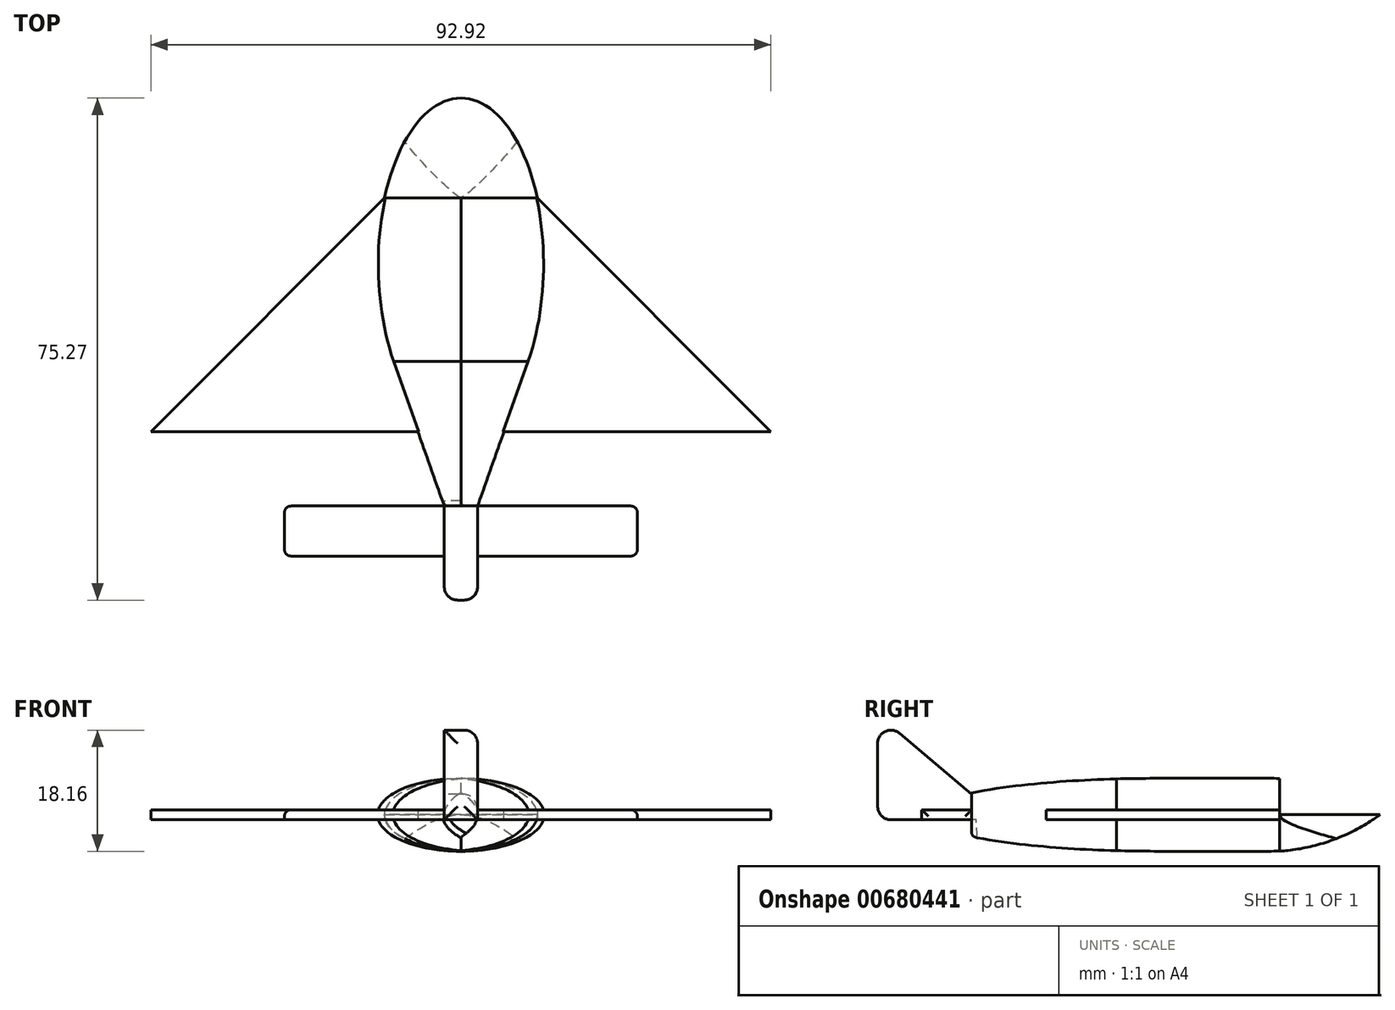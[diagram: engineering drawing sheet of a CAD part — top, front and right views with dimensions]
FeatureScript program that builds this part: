
annotation { "Feature Type Name" : "Feature", "Feature Type Description" : "" }
export const myFeature = defineFeature(function(context is Context, id is Id, definition is map)
    precondition{}
    {
        {
            var Q0;
            Q0=qCreatedBy(makeId("Top.planeOp"),FACE);
            var sketch = newSketch(context, id + "F0", { "sketchPlane" : qUnion([Q0])});
            skLineSegment(sketch, "E0", {"start": v(0, -25) * mm, "end": v(0, -47.8) * mm, "construction": true});
            skLineSegment(sketch, "E1", {"start": v(-2.5, -50.27) * mm, "end": v(2.5, -50.27) * mm});
            skLineSegment(sketch, "E2", {"start": v(-2.5, -50.27) * mm, "end": v(-2.5, -36.17) * mm});
            skLineSegment(sketch, "E3", {"start": v(2.5, -50.27) * mm, "end": v(2.5, -36.17) * mm});
            skLineSegment(sketch, "E4", {"start": v(-2.5, -36.17) * mm, "end": v(-10.2, -14.46) * mm});
            skLineSegment(sketch, "E5", {"start": v(2.5, -36.17) * mm, "end": v(10.2, -14.46) * mm});
            skLineSegment(sketch, "E6", {"start": v(0, 25) * mm, "end": v(0, 15) * mm});
            skLineSegment(sketch, "E7", {"start": v(0, 15) * mm, "end": v(0, 10) * mm});
            skLineSegment(sketch, "E8", {"start": v(-11.46, 10) * mm, "end": v(11.46, 10) * mm});
            skLineSegment(sketch, "E9", {"start": v(6.46, -25) * mm, "end": v(-6.46, -25) * mm});
            skLineSegment(sketch, "E10", {"start": v(-11.46, 10) * mm, "end": v(-46.46, -25) * mm});
            skLineSegment(sketch, "E11", {"start": v(-46.46, -25) * mm, "end": v(-6.46, -25) * mm});
            skLineSegment(sketch, "E12", {"start": v(0, -25) * mm, "end": v(0, -30) * mm});
            skLineSegment(sketch, "E13", {"start": v(-26.46, -36.17) * mm, "end": v(0, -36.17) * mm});
            skPoint(sketch, "E13.startSnap0", {"position": v(-26.46, -25) * mm});
            skLineSegment(sketch, "E14", {"start": v(-26.46, -36.17) * mm, "end": v(-26.46, -43.67) * mm});
            skLineSegment(sketch, "E15", {"start": v(-26.46, -43.67) * mm, "end": v(0, -43.67) * mm});
            skLineSegment(sketch, "E16", {"start": v(0, 10) * mm, "end": v(0, -25) * mm});
            skEllipticalArc(sketch, "E17", {});
            skEllipticalArc(sketch, "E18", {});
            skEllipticalArc(sketch, "E19", {});
            skEllipticalArc(sketch, "E20", {});
            skLineSegment(sketch, "E21", {"start": v(0, -36.17) * mm, "end": v(2.5, -36.17) * mm});
            skLineSegment(sketch, "E22.MirrorCS", {"start": v(26.46, -36.17) * mm, "end": v(0, -36.17) * mm});
            skLineSegment(sketch, "E23.MirrorCS", {"start": v(26.46, -43.67) * mm, "end": v(0, -43.67) * mm});
            skLineSegment(sketch, "E24.MirrorCS", {"start": v(26.46, -36.17) * mm, "end": v(26.46, -43.67) * mm});
            skLineSegment(sketch, "E25.MirrorCS", {"start": v(11.46, 10) * mm, "end": v(46.46, -25) * mm});
            skLineSegment(sketch, "E26.MirrorCS", {"start": v(46.46, -25) * mm, "end": v(6.46, -25) * mm});
            const initialGuessF0  = {"E17": [0, 0, 0, 1, 0.025, 0.0125, 1.1592794807274087, 2.187597417946572], "E18": [0, 0, 0, 1, 0.025, 0.0125, 5.1239058264521775, 0], "E19": [0, 0, 0, 1, 0.025, 0.0125, 4.095587889233014, 5.1239058264521775], "E20": [0, 0, 0, 1, 0.025, 0.0125, 0, 1.1592794807274087]};
            skSetInitialGuess(sketch, initialGuessF0);
            skSolve(sketch);
        }
        {
            var Q0;
            Q0=qCreatedBy(makeId("Front.planeOp"),FACE);
            var sketch = newSketch(context, id + "F1", { "sketchPlane" : qUnion([Q0])});
            skLineSegment(sketch, "E27.0", {"start": v(12.5, 0) * mm, "end": v(-12.5, 0) * mm});
            skEllipse(sketch, "E28", {"center": v(0, 0) * mm, "majorRadius": 12.5 * mm, "minorRadius": 5.47 * mm, "majorAxis": v(1, 0)});
            skSolve(sketch);
        }
        {
            var Q0;
            Q0=qCreatedBy(makeId("Front.planeOp"),FACE);
            cPlane(context, id + "F2", {"entities" : qUnion([Q0]), "cplaneType" : CPlaneType.OFFSET, "offset" : 25 * mm, "width" : 150 * mm, "height" : 150 * mm});
        }
        {
            var Q0;
            {var subQ0=sQuery(id+"F1.wireOp",EDGE,"E27.0");Q0=makeQuery(id+"F1.imprint","IMPRINT",FACE,{"disambiguationData":[TD([[makeQuery(id+"F1.imprint","IMPRINT",EDGE,{"derivedFrom":subQ0}),-1.0]])]});}
            var Q1;
            {var subQ0=sQuery(id+"F1.wireOp",EDGE,"E27.0");Q1=makeQuery(id+"F1.imprint","IMPRINT",FACE,{"disambiguationData":[TD([[makeQuery(id+"F1.imprint","IMPRINT",EDGE,{"derivedFrom":subQ0}),1.0]])]});}
            var Q2;
            Q2=sQuery(id+"F0.wireOp",EDGE,"E19");
            sweep(context, id + "F3", {"profiles" : qUnion([Q0, Q1]), "path" : qUnion([Q2]), "keepProfileOrientation" : true});
        }
        {
            var Q0;
            {var subQ0=sQuery(id+"F1.wireOp",EDGE,"E27.0");Q0=makeQuery(id+"F1.imprint","IMPRINT",FACE,{"disambiguationData":[TD([[makeQuery(id+"F1.imprint","IMPRINT",EDGE,{"derivedFrom":subQ0}),-1.0]])]});}
            var Q1;
            {var subQ0=sQuery(id+"F1.wireOp",EDGE,"E27.0");Q1=makeQuery(id+"F1.imprint","IMPRINT",FACE,{"disambiguationData":[TD([[makeQuery(id+"F1.imprint","IMPRINT",EDGE,{"derivedFrom":subQ0}),1.0]])]});}
            var Q2;
            Q2=sQuery(id+"F1.wireOp",EDGE,"E28");
            var Q3;
            Q3=sQuery(id+"F0.wireOp",EDGE,"E17");
            sweep(context, id + "F4", {"profiles" : qUnion([Q0, Q1]), "surfaceProfiles" : qUnion([Q2]), "path" : qUnion([Q3]), "keepProfileOrientation" : true});
        }
        {
            var Q0;
            Q0=makeQuery(id+"F4.opSweep","SWEPT_BODY",BODY,{"disambiguationData":[OSD([sQuery(id+"F0.wireOp",EDGE,"E17"),sQuery(id+"F1.wireOp",EDGE,"E27.0"),sQuery(id+"F1.wireOp",EDGE,"E28")])]});
            var Q1;
            Q1=makeQuery(id+"F3.opSweep","SWEPT_BODY",BODY,{"disambiguationData":[OSD([sQuery(id+"F0.wireOp",EDGE,"E19"),sQuery(id+"F1.wireOp",EDGE,"E27.0"),sQuery(id+"F1.wireOp",EDGE,"E28")])]});
            booleanBodies(context, id + "F5", {"operationType" : BooleanOperationType.INTERSECTION, "tools" : qUnion([Q0, Q1])});
        }
        {
            var Q0;
            Q0=makeQuery(id+"F4.opSweep","CAP_FACE",FACE,{"disambiguationData":[OSD([sQuery(id+"F0.wireOp",VERTEX,"E17.end"),sQuery(id+"F1.wireOp",EDGE,"E28")])],"isStart":false});
            var Q1;
            Q1=sQuery(id+"F0.wireOp",EDGE,"E4");
            sweep(context, id + "F6", {"profiles" : qUnion([Q0]), "path" : qUnion([Q1]), "keepProfileOrientation" : true});
        }
        {
            var Q0;
            Q0=makeQuery(id+"F4.opSweep","CAP_FACE",FACE,{"disambiguationData":[OSD([sQuery(id+"F0.wireOp",VERTEX,"E17.end"),sQuery(id+"F1.wireOp",EDGE,"E28")])],"isStart":false});
            var Q1;
            Q1=sQuery(id+"F0.wireOp",EDGE,"E5");
            sweep(context, id + "F7", {"profiles" : qUnion([Q0]), "path" : qUnion([Q1]), "keepProfileOrientation" : true});
        }
        {
            var Q0;
            Q0=makeQuery(id+"F6.opSweep","SWEPT_BODY",BODY,{"disambiguationData":[OSD([sQuery(id+"F0.wireOp",VERTEX,"E17.end"),sQuery(id+"F0.wireOp",EDGE,"E4"),sQuery(id+"F1.wireOp",EDGE,"E28")])]});
            var Q1;
            Q1=makeQuery(id+"F7.opSweep","SWEPT_BODY",BODY,{"disambiguationData":[OSD([sQuery(id+"F0.wireOp",VERTEX,"E17.end"),sQuery(id+"F0.wireOp",EDGE,"E5"),sQuery(id+"F1.wireOp",EDGE,"E28")])]});
            booleanBodies(context, id + "F8", {"operationType" : BooleanOperationType.INTERSECTION, "tools" : qUnion([Q0, Q1])});
        }
        {
            var Q0;
            {var subQ5=sQuery(id+"F0.wireOp",EDGE,"E24.MirrorCS");Q0=makeQuery(id+"F0.imprint","IMPRINT",FACE,{"disambiguationData":[TD([[makeQuery(id+"F0.imprint","IMPRINT",EDGE,{"derivedFrom":subQ5}),-1.0]])]});}
            var Q1;
            {var subQ1=sQuery(id+"F0.wireOp",EDGE,"E1");Q1=makeQuery(id+"F0.imprint","IMPRINT",FACE,{"disambiguationData":[TD([[makeQuery(id+"F0.imprint","IMPRINT",EDGE,{"derivedFrom":subQ1}),1.0]])]});}
            var Q2;
            {var subQ0=sQuery(id+"F0.wireOp",EDGE,"E23.MirrorCS");var subQ1=sQuery(id+"F0.wireOp",EDGE,"E15");var subQ2=makeQuery(id+"F0.imprint","INTERSECT",VERTEX,{"derivedFrom":[subQ1,subQ0]});Q2=makeQuery(id+"F0.imprint","IMPRINT",FACE,{"disambiguationData":[TD([[makeQuery(id+"F0.imprint","IMPRINT",EDGE,{"disambiguationData":[TD([[subQ2,1.0]])],"derivedFrom":subQ1}),1.0]])]});}
            var Q3;
            {var subQ5=sQuery(id+"F0.wireOp",EDGE,"E14");Q3=makeQuery(id+"F0.imprint","IMPRINT",FACE,{"disambiguationData":[TD([[makeQuery(id+"F0.imprint","IMPRINT",EDGE,{"derivedFrom":subQ5}),1.0]])]});}
            var Q4;
            {var subQ0=sQuery(id+"F1.wireOp",EDGE,"E28");Q4=makeQuery(id+"F8.opBoolean","INTERSECT",VERTEX,{"disambiguationData":[OD(1.0)],"derivedFrom":[makeQuery(id+"F6.opSweep","SWEPT_FACE",FACE,{"disambiguationData":[OSD([sQuery(id+"F0.wireOp",VERTEX,"E17.end"),sQuery(id+"F0.wireOp",EDGE,"E4"),subQ0])]}),makeQuery(id+"F7.opSweep","SWEPT_FACE",FACE,{"disambiguationData":[OSD([sQuery(id+"F0.wireOp",VERTEX,"E19.start"),sQuery(id+"F0.wireOp",EDGE,"E5"),subQ0])]})]});}
            extrude(context, id + "F9", {"entities" : qUnion([Q0, Q1, Q2, Q3]), "operationType" : NewBodyOperationType.ADD, "endBound" : BoundingType.SYMMETRIC, "depth" : 1.5 * mm, "endBoundEntityVertex" : qUnion([Q4]), "offsetDistance" : 25 * mm});
        }
        {
            var Q0;
            Q0=makeQuery(id+"F0.imprint","IMPRINT",FACE,{"disambiguationData":[TD([[makeQuery(id+"F0.imprint","IMPRINT",EDGE,{"derivedFrom":sQuery(id+"F0.wireOp",EDGE,"E6")}),1.0]])]});
            var Q1;
            Q1=makeQuery(id+"F0.imprint","IMPRINT",FACE,{"disambiguationData":[TD([[makeQuery(id+"F0.imprint","IMPRINT",EDGE,{"derivedFrom":sQuery(id+"F0.wireOp",EDGE,"E6")}),-1.0]])]});
            extrude(context, id + "F10", {"entities" : qUnion([Q0, Q1]), "oppositeDirection" : true, "depth" : 25 * mm, "offsetDistance" : 25 * mm});
        }
        {
            var Q0;
            Q0=makeQuery(id+"F4.opSweep","CAP_FACE",FACE,{"disambiguationData":[OSD([sQuery(id+"F0.wireOp",VERTEX,"E17.start"),sQuery(id+"F1.wireOp",EDGE,"E28")])],"isStart":true});
            extrude(context, id + "F11", {"entities" : qUnion([Q0]), "depth" : 25 * mm, "offsetDistance" : 25 * mm});
        }
        {
            var Q0;
            Q0=qCreatedBy(makeId("Right.planeOp"),FACE);
            var sketch = newSketch(context, id + "F12", { "sketchPlane" : qUnion([Q0])});
            skPoint(sketch, "E29.0", {"position": v(10, -5.45) * mm});
            skPoint(sketch, "E30.0", {"position": v(25, 0) * mm});
            skArc(sketch, "E31", {"start": v(10, -5.45) * mm, "mid": v(17.89, -3.8) * mm, "end": v(25, 0) * mm});
            skLineSegment(sketch, "E32", {"start": v(10, -5.45) * mm, "end": v(10, 0) * mm});
            skLineSegment(sketch, "E33", {"start": v(10, 0) * mm, "end": v(25, 0) * mm});
            skSolve(sketch);
        }
        {
            var Q0;
            Q0 = qSketchRegion(id + "F12", true);
            extrude(context, id + "F13", {"entities" : qUnion([Q0]), "endBound" : BoundingType.SYMMETRIC, "depth" : 100 * mm, "offsetDistance" : 25 * mm});
        }
        {
            var Q0;
            Q0=makeQuery(id+"F10.opExtrude","SWEPT_BODY",BODY,{"disambiguationData":[OSD([sQuery(id+"F0.wireOp",EDGE,"E8"),sQuery(id+"F0.wireOp",EDGE,"E18"),sQuery(id+"F0.wireOp",EDGE,"E20")])]});
            var Q1;
            Q1=makeQuery(id+"F11.opExtrude","SWEPT_BODY",BODY,{"disambiguationData":[OSD([sQuery(id+"F0.wireOp",VERTEX,"E17.start"),sQuery(id+"F1.wireOp",EDGE,"E28")])]});
            var Q2;
            Q2=makeQuery(id+"F13.opExtrude","SWEPT_BODY",BODY,{"disambiguationData":[OSD([sQuery(id+"F12.wireOp",EDGE,"E31"),sQuery(id+"F12.wireOp",EDGE,"E32"),sQuery(id+"F12.wireOp",EDGE,"E33")])]});
            booleanBodies(context, id + "F14", {"operationType" : BooleanOperationType.INTERSECTION, "tools" : qUnion([Q0, Q1, Q2])});
        }
        {
            var Q0;
            Q0=qCreatedBy(makeId("Top.planeOp"),FACE);
            var sketch = newSketch(context, id + "F15", { "sketchPlane" : qUnion([Q0])});
            skPoint(sketch, "E34.0", {"position": v(-46.46, -25) * mm});
            skPoint(sketch, "E35.0", {"position": v(46.46, -25) * mm});
            skPoint(sketch, "E36.0", {"position": v(11.46, 10) * mm});
            skPoint(sketch, "E37.0", {"position": v(-11.46, 10) * mm});
            skLineSegment(sketch, "E38", {"start": v(-46.46, -25) * mm, "end": v(46.46, -25) * mm});
            skLineSegment(sketch, "E39", {"start": v(11.46, 10) * mm, "end": v(-11.46, 10) * mm});
            skLineSegment(sketch, "E40", {"start": v(-46.46, -25) * mm, "end": v(-11.46, 10) * mm});
            skLineSegment(sketch, "E41", {"start": v(11.46, 10) * mm, "end": v(46.46, -25) * mm});
            skLineSegment(sketch, "E42", {"start": v(46.46, -25) * mm, "end": v(-46.46, -25) * mm});
            skSolve(sketch);
        }
        {
            var Q0;
            Q0=makeQuery(id+"F15.imprint","IMPRINT",FACE,{"disambiguationData":[TD([[makeQuery(id+"F15.imprint","IMPRINT",EDGE,{"derivedFrom":sQuery(id+"F15.wireOp",EDGE,"E39")}),1.0]])]});
            extrude(context, id + "F16", {"entities" : qUnion([Q0]), "operationType" : NewBodyOperationType.ADD, "endBound" : BoundingType.SYMMETRIC, "depth" : 1.5 * mm, "offsetDistance" : 25 * mm});
        }
        {
            var Q0;
            {var subQ0=sQuery(id+"F0.wireOp",EDGE,"E23.MirrorCS");var subQ1=sQuery(id+"F0.wireOp",EDGE,"E15");var subQ2=makeQuery(id+"F0.imprint","INTERSECT",VERTEX,{"derivedFrom":[subQ1,subQ0]});Q0=makeQuery(id+"F0.imprint","IMPRINT",FACE,{"disambiguationData":[TD([[makeQuery(id+"F0.imprint","IMPRINT",EDGE,{"disambiguationData":[TD([[subQ2,1.0]])],"derivedFrom":subQ1}),1.0]])]});}
            var Q1;
            {var subQ1=sQuery(id+"F0.wireOp",EDGE,"E1");Q1=makeQuery(id+"F0.imprint","IMPRINT",FACE,{"disambiguationData":[TD([[makeQuery(id+"F0.imprint","IMPRINT",EDGE,{"derivedFrom":subQ1}),1.0]])]});}
            extrude(context, id + "F17", {"entities" : qUnion([Q0, Q1]), "operationType" : NewBodyOperationType.ADD, "depth" : 15 * mm, "offsetDistance" : 25 * mm});
        }
        {
            var Q0;
            {var subQ0=sQuery(id+"F0.wireOp",EDGE,"E2");Q0=makeQuery(id+"F17.boolean.opBoolean","MERGE",FACE,{"derivedFrom":[makeQuery(id+"F9.opExtrude","SWEPT_FACE",FACE,{"disambiguationData":[OSD([subQ0])]}),makeQuery(id+"F17.opExtrude","SWEPT_FACE",FACE,{"disambiguationData":[OSD([subQ0])]})]});}
            var sketch = newSketch(context, id + "F18", { "sketchPlane" : qUnion([Q0])});
            skLineSegment(sketch, "E43", {"start": v(50.27, 15) * mm, "end": v(36.17, 3.06) * mm});
            skLineSegment(sketch, "E44", {"start": v(36.17, 3.06) * mm, "end": v(36.17, 15) * mm});
            skLineSegment(sketch, "E45", {"start": v(36.17, 15) * mm, "end": v(50.27, 15) * mm});
            skSolve(sketch);
        }
        {
            var Q0;
            Q0=makeQuery(id+"F18.imprint","IMPRINT",FACE,{"disambiguationData":[TD([[makeQuery(id+"F18.imprint","IMPRINT",EDGE,{"derivedFrom":sQuery(id+"F18.wireOp",EDGE,"E43")}),-1.0]])]});
            extrude(context, id + "F19", {"entities" : qUnion([Q0]), "operationType" : NewBodyOperationType.REMOVE, "oppositeDirection" : true, "depth" : 25 * mm, "offsetDistance" : 25 * mm});
        }
        {
            var Q0;
            {var subQ0=sQuery(id+"F0.wireOp",EDGE,"E1");Q0=makeQuery(id+"F19.boolean.opBoolean","MERGE",EDGE,{"derivedFrom":[makeQuery(id+"F17.opExtrude","CAP_EDGE",EDGE,{"disambiguationData":[OSD([subQ0])],"isStart":false}),makeQuery(id+"F19.opExtrude","SWEPT_EDGE",EDGE,{"disambiguationData":[OSD([subQ0,sQuery(id+"F0.wireOp",EDGE,"E2"),sQuery(id+"F18.wireOp",EDGE,"E43"),sQuery(id+"F18.wireOp",EDGE,"E45")])]})]});}
            var Q1;
            Q1=makeQuery(id+"F9.opExtrude","CAP_EDGE",EDGE,{"disambiguationData":[OSD([sQuery(id+"F0.wireOp",EDGE,"E1")])],"isStart":true});
            var Q2;
            Q2=makeQuery(id+"F19.boolean.opBoolean","COPY",EDGE,{"derivedFrom":makeQuery(id+"F19.opExtrude","CAP_EDGE",EDGE,{"disambiguationData":[OSD([sQuery(id+"F18.wireOp",EDGE,"E43")])],"isStart":true})});
            var Q3;
            {var subQ0=sQuery(id+"F0.wireOp",EDGE,"E3");Q3=makeQuery(id+"F19.boolean.opBoolean","INTERSECT",EDGE,{"derivedFrom":[makeQuery(id+"F17.boolean.opBoolean","MERGE",FACE,{"derivedFrom":[makeQuery(id+"F9.opExtrude","SWEPT_FACE",FACE,{"disambiguationData":[OSD([subQ0])]}),makeQuery(id+"F17.opExtrude","SWEPT_FACE",FACE,{"disambiguationData":[OSD([subQ0])]})]}),makeQuery(id+"F19.opExtrude","SWEPT_FACE",FACE,{"disambiguationData":[OSD([sQuery(id+"F18.wireOp",EDGE,"E43")])]})]});}
            var Q4;
            {var subQ0=sQuery(id+"F0.wireOp",EDGE,"E2");var subQ1=sQuery(id+"F0.wireOp",EDGE,"E1");Q4=makeQuery(id+"F17.boolean.opBoolean","MERGE",EDGE,{"derivedFrom":[makeQuery(id+"F9.opExtrude","SWEPT_EDGE",EDGE,{"disambiguationData":[OSD([subQ1,subQ0])]}),makeQuery(id+"F17.opExtrude","SWEPT_EDGE",EDGE,{"disambiguationData":[OSD([subQ1,subQ0])]})]});}
            var Q5;
            {var subQ0=sQuery(id+"F0.wireOp",EDGE,"E3");var subQ1=sQuery(id+"F0.wireOp",EDGE,"E1");Q5=makeQuery(id+"F17.boolean.opBoolean","MERGE",EDGE,{"derivedFrom":[makeQuery(id+"F9.opExtrude","SWEPT_EDGE",EDGE,{"disambiguationData":[OSD([subQ1,subQ0])]}),makeQuery(id+"F17.opExtrude","SWEPT_EDGE",EDGE,{"disambiguationData":[OSD([subQ1,subQ0])]})]});}
            fillet(context, id + "F20", {"entities" : qUnion([Q0, Q1, Q2, Q3, Q4, Q5]), "radius" : 2 * mm, "tangentPropagation" : true, "allowEdgeOverflow" : false});
        }
        {
            var Q0;
            Q0=makeQuery(id+"F9.opExtrude","SWEPT_EDGE",EDGE,{"disambiguationData":[OSD([sQuery(id+"F0.wireOp",EDGE,"E14"),sQuery(id+"F0.wireOp",EDGE,"E15")])]});
            var Q1;
            Q1=makeQuery(id+"F9.opExtrude","SWEPT_EDGE",EDGE,{"disambiguationData":[OSD([sQuery(id+"F0.wireOp",EDGE,"E13"),sQuery(id+"F0.wireOp",EDGE,"E14")])]});
            var Q2;
            Q2=makeQuery(id+"F9.opExtrude","SWEPT_EDGE",EDGE,{"disambiguationData":[OSD([sQuery(id+"F0.wireOp",EDGE,"E22.MirrorCS"),sQuery(id+"F0.wireOp",EDGE,"E24.MirrorCS")])]});
            var Q3;
            Q3=makeQuery(id+"F9.opExtrude","SWEPT_EDGE",EDGE,{"disambiguationData":[OSD([sQuery(id+"F0.wireOp",EDGE,"E23.MirrorCS"),sQuery(id+"F0.wireOp",EDGE,"E24.MirrorCS")])]});
            var Q4;
            Q4=makeQuery(id+"F9.opExtrude","CAP_EDGE",EDGE,{"disambiguationData":[OSD([sQuery(id+"F0.wireOp",EDGE,"E14")])],"isStart":false});
            var Q5;
            Q5=makeQuery(id+"F9.opExtrude","CAP_EDGE",EDGE,{"disambiguationData":[OSD([sQuery(id+"F0.wireOp",EDGE,"E24.MirrorCS")])],"isStart":false});
            fillet(context, id + "F21", {"entities" : qUnion([Q0, Q1, Q2, Q3, Q4, Q5]), "radius" : 1 * mm, "tangentPropagation" : true, "allowEdgeOverflow" : false});
        }
        {
            var Q0;
            {var subQ0=sQuery(id+"F0.wireOp",EDGE,"E22.MirrorCS");var subQ1=sQuery(id+"F0.wireOp",EDGE,"E13");var subQ2=sQuery(id+"F1.wireOp",EDGE,"E28");var subQ3=sQuery(id+"F0.wireOp",VERTEX,"E19.start");var subQ4=makeQuery(id+"F7.opSweep","SWEPT_FACE",FACE,{"disambiguationData":[OSD([subQ3,sQuery(id+"F0.wireOp",EDGE,"E5"),subQ2])]});var subQ5=sQuery(id+"F0.wireOp",VERTEX,"E17.end");var subQ6=makeQuery(id+"F6.opSweep","CAP_FACE",FACE,{"disambiguationData":[OSD([sQuery(id+"F0.wireOp",VERTEX,"E4.start"),subQ5,subQ2])],"isStart":false});Q0=makeQuery(id+"F9.boolean.opBoolean","SPLIT",EDGE,{"disambiguationData":[topologyDisambiguationEdgeConnected([subQ6,subQ4]),TD([makeQuery(id+"F9.opExtrude","CAP_FACE",FACE,{"disambiguationData":[OSD([sQuery(id+"F0.wireOp",EDGE,"E1"),sQuery(id+"F0.wireOp",EDGE,"E2"),sQuery(id+"F0.wireOp",EDGE,"E3"),subQ1,sQuery(id+"F0.wireOp",EDGE,"E14"),sQuery(id+"F0.wireOp",EDGE,"E15"),subQ0,sQuery(id+"F0.wireOp",EDGE,"E23.MirrorCS"),sQuery(id+"F0.wireOp",EDGE,"E24.MirrorCS")])],"isStart":true})])],"derivedFrom":makeQuery(id+"F7.opSweep","CAP_EDGE",EDGE,{"disambiguationData":[OSD([sQuery(id+"F0.wireOp",VERTEX,"E5.start"),subQ3,subQ2])],"isStart":false})});}
            var Q1;
            {var subQ0=sQuery(id+"F0.wireOp",EDGE,"E22.MirrorCS");var subQ1=sQuery(id+"F0.wireOp",EDGE,"E13");var subQ2=sQuery(id+"F1.wireOp",EDGE,"E28");var subQ3=sQuery(id+"F0.wireOp",VERTEX,"E17.end");var subQ4=makeQuery(id+"F6.opSweep","SWEPT_FACE",FACE,{"disambiguationData":[OSD([subQ3,sQuery(id+"F0.wireOp",EDGE,"E4"),subQ2])]});var subQ5=sQuery(id+"F0.wireOp",VERTEX,"E4.start");var subQ6=makeQuery(id+"F6.opSweep","CAP_FACE",FACE,{"disambiguationData":[OSD([subQ5,subQ3,subQ2])],"isStart":false});Q1=makeQuery(id+"F9.boolean.opBoolean","SPLIT",EDGE,{"disambiguationData":[topologyDisambiguationEdgeConnected([subQ6,subQ4]),TD([makeQuery(id+"F9.opExtrude","CAP_FACE",FACE,{"disambiguationData":[OSD([sQuery(id+"F0.wireOp",EDGE,"E1"),sQuery(id+"F0.wireOp",EDGE,"E2"),sQuery(id+"F0.wireOp",EDGE,"E3"),subQ1,sQuery(id+"F0.wireOp",EDGE,"E14"),sQuery(id+"F0.wireOp",EDGE,"E15"),subQ0,sQuery(id+"F0.wireOp",EDGE,"E23.MirrorCS"),sQuery(id+"F0.wireOp",EDGE,"E24.MirrorCS")])],"isStart":true})])],"derivedFrom":makeQuery(id+"F6.opSweep","CAP_EDGE",EDGE,{"disambiguationData":[OSD([subQ5,subQ3,subQ2])],"isStart":false})});}
            fillet(context, id + "F22", {"entities" : qUnion([Q0, Q1]), "radius" : 1 * mm, "tangentPropagation" : true, "allowEdgeOverflow" : false});
        }
    });
